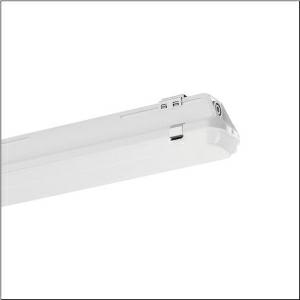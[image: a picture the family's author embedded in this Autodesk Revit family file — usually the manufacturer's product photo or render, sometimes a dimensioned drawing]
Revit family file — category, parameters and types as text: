
# Revit family: monsun_21_51fb107l420k
name_source: partatom
category: Lighting Fixtures
units: mm (PartAtom-declared; Revit-internal decimal feet)

## family parameters
Cut with Voids When Loaded = No
Host = Face
Light Source = No
Part Type = Normal
Room Calculation Point = No
Round Connector Dimension = Use Diameter
Shared = No

## types (1)
- Monsun 21 (1 x LED, 2590 lm, 15.6 W, 4000K)
    Apparent Load = 16 VA
    CIE Flux Codes = 46 76 93 94 100
    Color Rendering = 80
    Color Temperature = 4000K
    Default Elevation = 1800 mm
    Description = Monsun 21, damp-proof luminaire, chain hanger, primary optical cover: enclosure, of PMMA, light emission: direct distribution, primary light characteristic: symmetric, installation type: vertical mounting, horizontal mounting, surface-mounted, suspended mounting, LED, rated luminous flux: 2.590lm, luminous efficacy: 166lm/W, light colour: 840, colour temperature: 4000K, control gear: ON/OFF, with terminal, 3-pole, max. 2.5mm², mains connection: 220..240V, AC, 50/60Hz, rated input power: 16W, housing, of glass-fibre reinforced plastic, uncoated, bright grey, incl. chain hanger, length: 1.299mm, width: 90mm, height: 88mm, clip for enclosure, of stainless steel (V2A), ceiling mounting element, of stainless steel (V2A), chain hanger, of stainless steel (V2A), protection rating (complete): IP66, insulation class (complete): insulation class I (protective earthing), certification: CE, ENEC, VDE, UKCA, protection symbol: D, impact resistance: IK04, permissible operating ambient temperature: -25..+35°C, standard: EN 50419, EN 60598-2-1, corresponds to IFS (International Featured Standards) requirements for safety and quality in the food industry, for indoor or canopied outdoor use, no direct snow, no direct sun, no direct rain, LABS conformity tested according to VDMA 24364:2018-05, contact your sales advisor before using the luminaires in applications with unclear chemical exposure, large temperature fluctuations or condensation-forming humidity, packaging unit: 1 piece
    Height = 88 mm
    Lamp = 1 x LED
    Lamp Light Flux = 2590 lm
    Lamp Power = 15.6 W
    Lamp count = 1
    Length = 1299 mm
    Luminous efficacy = 166 lm/W
    Manufacturer = Siteco
    ModVariant = No
    Model = 51FB107L420K
    Mounting Place = Ceiling
    Mounting Type = Surface mounted
    Number of Poles = 1
    OnlyDefault = Yes
    Power Factor = 1
    Product Name = Monsun 21
    Product group = damp-proof luminaire
    ProductGroupID = 300
    Protection Class = Protection class I
    Protection Degree = IP 66
    RLX_Detail_Level = 1
    RLX_Emergency_Light_Flux = 0 lm
    RLX_Emergency_Type = 0
    RLX_Emergency_Type_DB = No
    RlxData = <blob elided: 89557 chars, md5=f1208e3e>
    Socket = socket
    Standby Power = 0 W
    System Light Flux = 2590 lm
    System Power = 16 W
    Type Comments = Product without accessories
    Type Image = l_1319656.jpg
    URL = http://relux.com
    VarID = ---
    Voltage = 0 V
    Weight = 0.00 kg
    Width = 90 mm

## geometry (parser evidence)
native form markers: Blend x4, Sweep x13
no freeform markers — native parametric forms only
